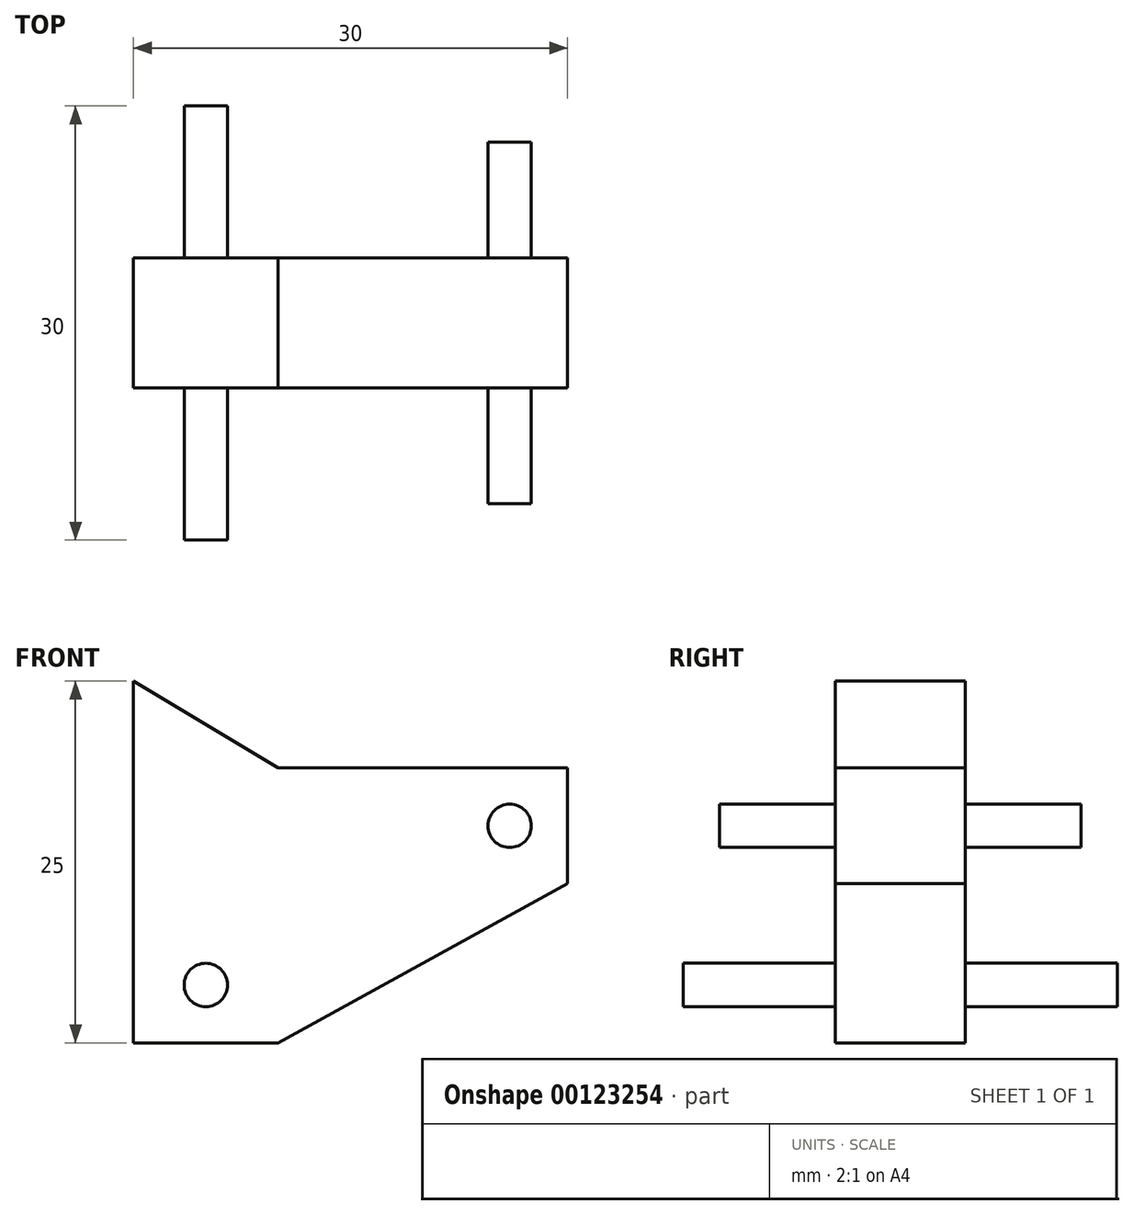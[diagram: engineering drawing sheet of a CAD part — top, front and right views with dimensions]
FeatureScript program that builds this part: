
annotation { "Feature Type Name" : "Feature", "Feature Type Description" : "" }
export const myFeature = defineFeature(function(context is Context, id is Id, definition is map)
    precondition{}
    {
        {
            var Q0;
            Q0=qCreatedBy(makeId("Front.planeOp"),FACE);
            var sketch = newSketch(context, id + "F0", { "sketchPlane" : qUnion([Q0])});
            skLineSegment(sketch, "E0", {"start": v(-10.4, 17.3) * mm, "end": v(-0.4, 11.3) * mm});
            skLineSegment(sketch, "E1", {"start": v(-0.4, 11.3) * mm, "end": v(19.6, 11.3) * mm});
            skLineSegment(sketch, "E2", {"start": v(19.6, 11.3) * mm, "end": v(19.6, 3.3) * mm});
            skLineSegment(sketch, "E3", {"start": v(19.6, 3.3) * mm, "end": v(-0.4, -7.7) * mm});
            skLineSegment(sketch, "E4", {"start": v(-0.4, -7.7) * mm, "end": v(-10.4, -7.7) * mm});
            skLineSegment(sketch, "E5", {"start": v(-10.4, -7.7) * mm, "end": v(-10.4, 17.3) * mm});
            skCircle(sketch, "E6", {"center": v(15.6, 7.3) * mm, "radius": 1.5 * mm});
            skCircle(sketch, "E7", {"center": v(-5.4, -3.7) * mm, "radius": 1.5 * mm});
            skSolve(sketch);
        }
        {
            var Q0;
            Q0=makeQuery(id+"F0.imprint","IMPRINT",FACE,{"disambiguationData":[TD([[makeQuery(id+"F0.imprint","IMPRINT",EDGE,{"derivedFrom":sQuery(id+"F0.wireOp",EDGE,"E0")}),-1.0]])]});
            extrude(context, id + "F1", {"entities" : qUnion([Q0]), "endBound" : BoundingType.SYMMETRIC, "depth" : 9 * mm});
        }
        {
            var Q0;
            Q0=makeQuery(id+"F0.imprint","IMPRINT",FACE,{"disambiguationData":[TD([[makeQuery(id+"F0.imprint","IMPRINT",EDGE,{"derivedFrom":sQuery(id+"F0.wireOp",EDGE,"E7")}),1.0]])]});
            extrude(context, id + "F2", {"entities" : qUnion([Q0]), "operationType" : NewBodyOperationType.ADD, "endBound" : BoundingType.SYMMETRIC, "depth" : 30 * mm});
        }
        {
            var Q0;
            Q0=makeQuery(id+"F0.imprint","IMPRINT",FACE,{"disambiguationData":[TD([[makeQuery(id+"F0.imprint","IMPRINT",EDGE,{"derivedFrom":sQuery(id+"F0.wireOp",EDGE,"E6")}),1.0]])]});
            extrude(context, id + "F3", {"entities" : qUnion([Q0]), "operationType" : NewBodyOperationType.ADD, "endBound" : BoundingType.SYMMETRIC, "depth" : 25 * mm});
        }
    });
